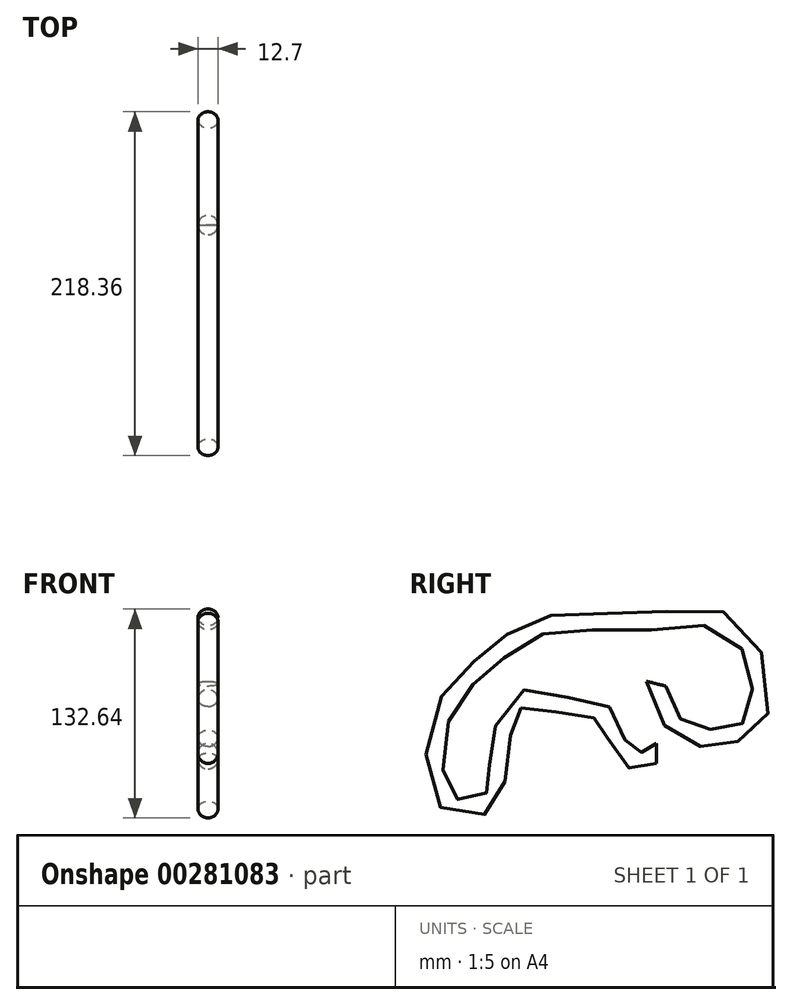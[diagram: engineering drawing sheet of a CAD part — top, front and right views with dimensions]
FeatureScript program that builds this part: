
annotation { "Feature Type Name" : "Feature", "Feature Type Description" : "" }
export const myFeature = defineFeature(function(context is Context, id is Id, definition is map)
    precondition{}
    {
        {
            var Q0;
            Q0=qCreatedBy(makeId("Right.planeOp"),FACE);
            var sketch = newSketch(context, id + "F0", { "sketchPlane" : qUnion([Q0])});
            skFitSpline(sketch, "E0", {"points": [v(0, 0) * mm, v(-8.7, -4) * mm, v(-22.12, 0) * mm, v(-29.65, 22.12) * mm, v(-59.3, 30.83) * mm, v(-87.8, 32.8) * mm, v(-100.46, -6.77) * mm, v(-107.58, -31.7) * mm, v(-133.3, -30.12) * mm, v(-135.29, 26.47) * mm, v(-107.19, 58.53) * mm, v(-73.55, 80.7) * mm, v(-4.3, 83.86) * mm, v(52.3, 78.32) * mm, v(64.18, 21.33) * mm, v(46.37, 12.23) * mm, v(18.66, 11.83) * mm, v(0, 44.28) * mm], "startDerivative": vector(-243.37, -160.29) * mm, "endDerivative": vector(-235.12, 673.83) * mm});
            skSolve(sketch);
        }
        {
            var Q0;
            Q0=qCreatedBy(makeId("Front.planeOp"),FACE);
            var sketch = newSketch(context, id + "F1", { "sketchPlane" : qUnion([Q0])});
            skCircle(sketch, "E1", {"center": v(0, 0) * mm, "radius": 6.35 * mm});
            skSolve(sketch);
        }
        {
            var Q0;
            Q0=makeQuery(id+"F1.imprint","IMPRINT",FACE,{"disambiguationData":[TD([[makeQuery(id+"F1.imprint","IMPRINT",EDGE,{"derivedFrom":sQuery(id+"F1.wireOp",EDGE,"E1")}),1.0]])]});
            var Q1;
            Q1=sQuery(id+"F0.wireOp",EDGE,"E0");
            sweep(context, id + "F2", {"profiles" : qUnion([Q0]), "path" : qUnion([Q1])});
        }
    });
